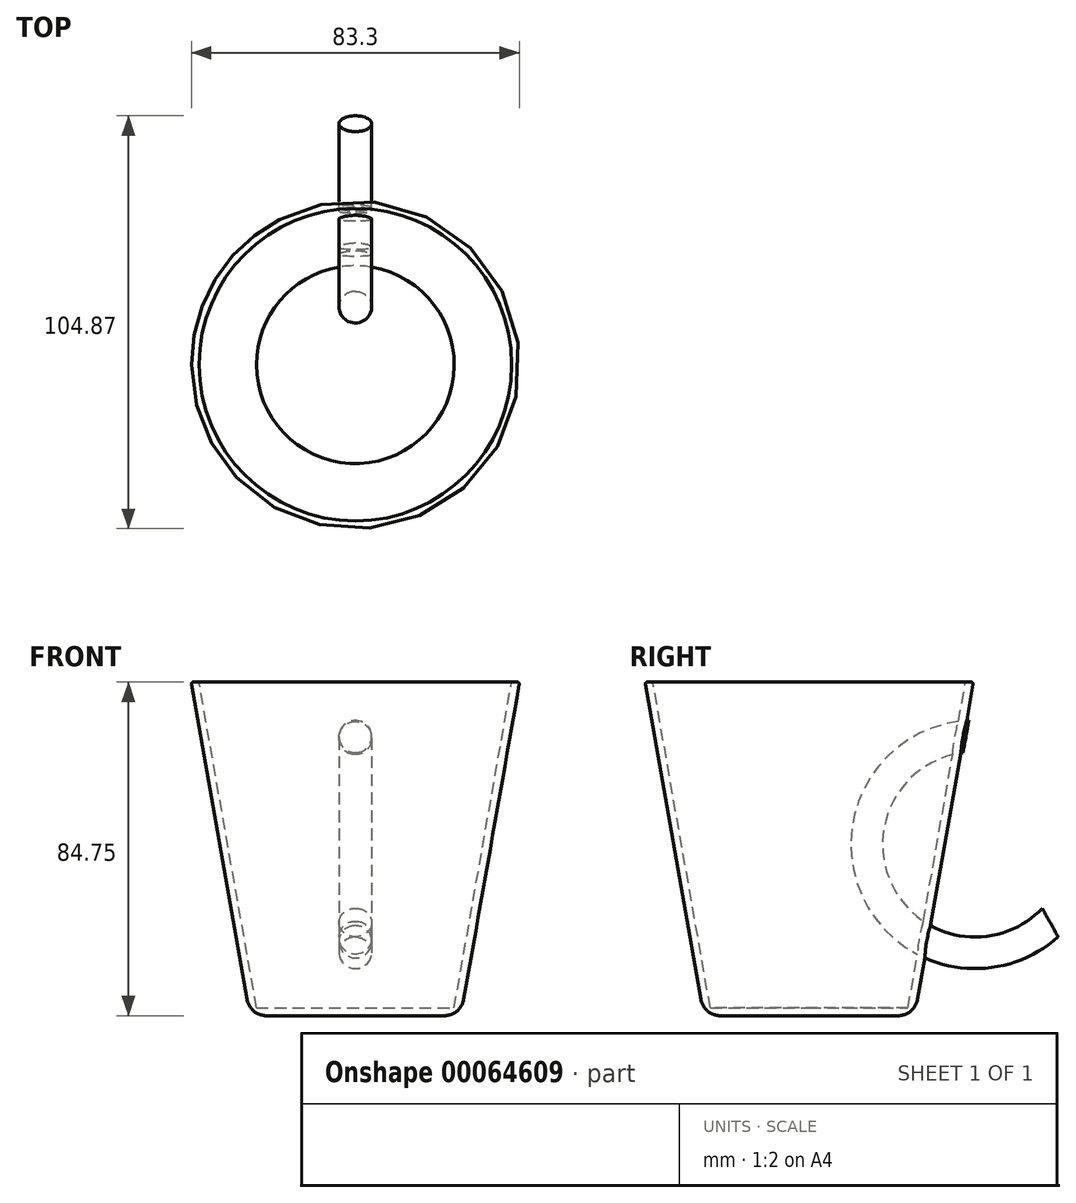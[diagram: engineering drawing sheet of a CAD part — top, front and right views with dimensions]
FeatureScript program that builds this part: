
annotation { "Feature Type Name" : "Feature", "Feature Type Description" : "" }
export const myFeature = defineFeature(function(context is Context, id is Id, definition is map)
    precondition{}
    {
        {
            var Q0;
            Q0=qCreatedBy(makeId("Front.planeOp"),FACE);
            var sketch = newSketch(context, id + "F0", { "sketchPlane" : qUnion([Q0])});
            skLineSegment(sketch, "E0", {"start": v(0, 0) * mm, "end": v(26.8, 0) * mm});
            skLineSegment(sketch, "E1", {"start": v(26.8, 0) * mm, "end": v(41.74, 84.75) * mm});
            skLineSegment(sketch, "E2", {"start": v(0, 0) * mm, "end": v(0, 84.75) * mm});
            skLineSegment(sketch, "E3", {"start": v(0, 84.75) * mm, "end": v(41.74, 84.75) * mm});
            skSolve(sketch);
        }
        {
            var Q0;
            Q0 = qSketchRegion(id + "F0", true);
            var Q1;
            Q1=sQuery(id+"F0.wireOp",EDGE,"E2");
            revolve(context, id + "F1", {"entities" : qUnion([Q0]), "axis" : qUnion([Q1]), "revolveType" : RevolveType.FULL});
        }
        {
            var Q0;
            Q0=makeQuery(id+"F1.opRevolve","SWEPT_FACE",FACE,{"disambiguationData":[OSD([sQuery(id+"F0.wireOp",EDGE,"E3")])]});
            shell(context, id + "F2", {"entities" : qUnion([Q0]), "thickness" : 2 * mm});
        }
        {
            var Q0;
            Q0=makeQuery(id+"F1.opRevolve","SWEPT_EDGE",EDGE,{"disambiguationData":[OSD([sQuery(id+"F0.wireOp",EDGE,"E1"),sQuery(id+"F0.wireOp",EDGE,"E3")])]});
            fillet(context, id + "F3", {"entities" : qUnion([Q0]), "radius" : 0.5 * mm, "tangentPropagation" : true, "allowEdgeOverflow" : false});
        }
        {
            var Q0;
            Q0=makeQuery(id+"F1.opRevolve","SWEPT_EDGE",EDGE,{"disambiguationData":[OSD([sQuery(id+"F0.wireOp",EDGE,"E0"),sQuery(id+"F0.wireOp",EDGE,"E1")])]});
            fillet(context, id + "F4", {"entities" : qUnion([Q0]), "radius" : 5 * mm, "tangentPropagation" : true, "allowEdgeOverflow" : false});
        }
        {
            var Q0;
            Q0=qCreatedBy(makeId("Front.planeOp"),FACE);
            cPlane(context, id + "F5", {"entities" : qUnion([Q0]), "cplaneType" : CPlaneType.OFFSET, "offset" : 35 * mm, "oppositeDirection" : true, "width" : 150 * mm, "height" : 150 * mm});
        }
        {
            var Q0;
            Q0=qCreatedBy(id+"F5.planeOp",FACE);
            var sketch = newSketch(context, id + "F6", { "sketchPlane" : qUnion([Q0])});
            skCircle(sketch, "E4", {"center": v(0, 70.07) * mm, "radius": 4.16 * mm});
            skSolve(sketch);
        }
        {
            var Q0;
            Q0=qCreatedBy(makeId("Right.planeOp"),FACE);
            var sketch = newSketch(context, id + "F7", { "sketchPlane" : qUnion([Q0])});
            skArc(sketch, "E5", {"start": v(30.36, 18.34) * mm, "mid": v(69.8, 40.8) * mm, "end": v(35.47, 70.48) * mm});
            skSolve(sketch);
        }
        {
            var Q0;
            Q0 = qSketchRegion(id + "F6", true);
            var Q1;
            Q1 = qConstructionFilter(qBodyType(qCreatedBy(id + "F7" ,EDGE), BodyType.WIRE), ConstructionObject.NO);
            sweep(context, id + "F8", {"operationType" : NewBodyOperationType.ADD, "profiles" : qUnion([Q0]), "path" : qUnion([Q1])});
        }
    });
